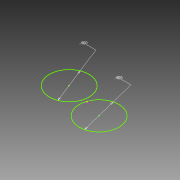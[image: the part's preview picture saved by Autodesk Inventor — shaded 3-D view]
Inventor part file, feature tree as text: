
AUTODESK INVENTOR PART (.ipt)
format: ipt  version: 2015 (Build 190159000, 159)  size: 147,456 bytes
history: native  units: in
note: dims shown in document units (in); Inventor stores cm internally (conversion verified against a paired STEP export)
features: sketch x3, plane x1, sweep x1, other x1
ambient origin geometry x8: Origin, YZ Plane, XZ Plane, XY Plane, X Axis, Y Axis, Z Axis, Center Point
bodies: Solid1 (feature_tree)
feature tree (6):
  sketch  "Sketch3"  dims[d0=0.4in d1=0.4in]
  sketch  "Sketch4"  dims[d2=0.404in]
  plane  "Work Plane1"
  sweep  "Sweep1"
  other  "Image1"
  sketch  "Sketch5"  dims[d3=0.1in d4=0.06in d5=0.06in d18=0.0in d19=0.0in]
